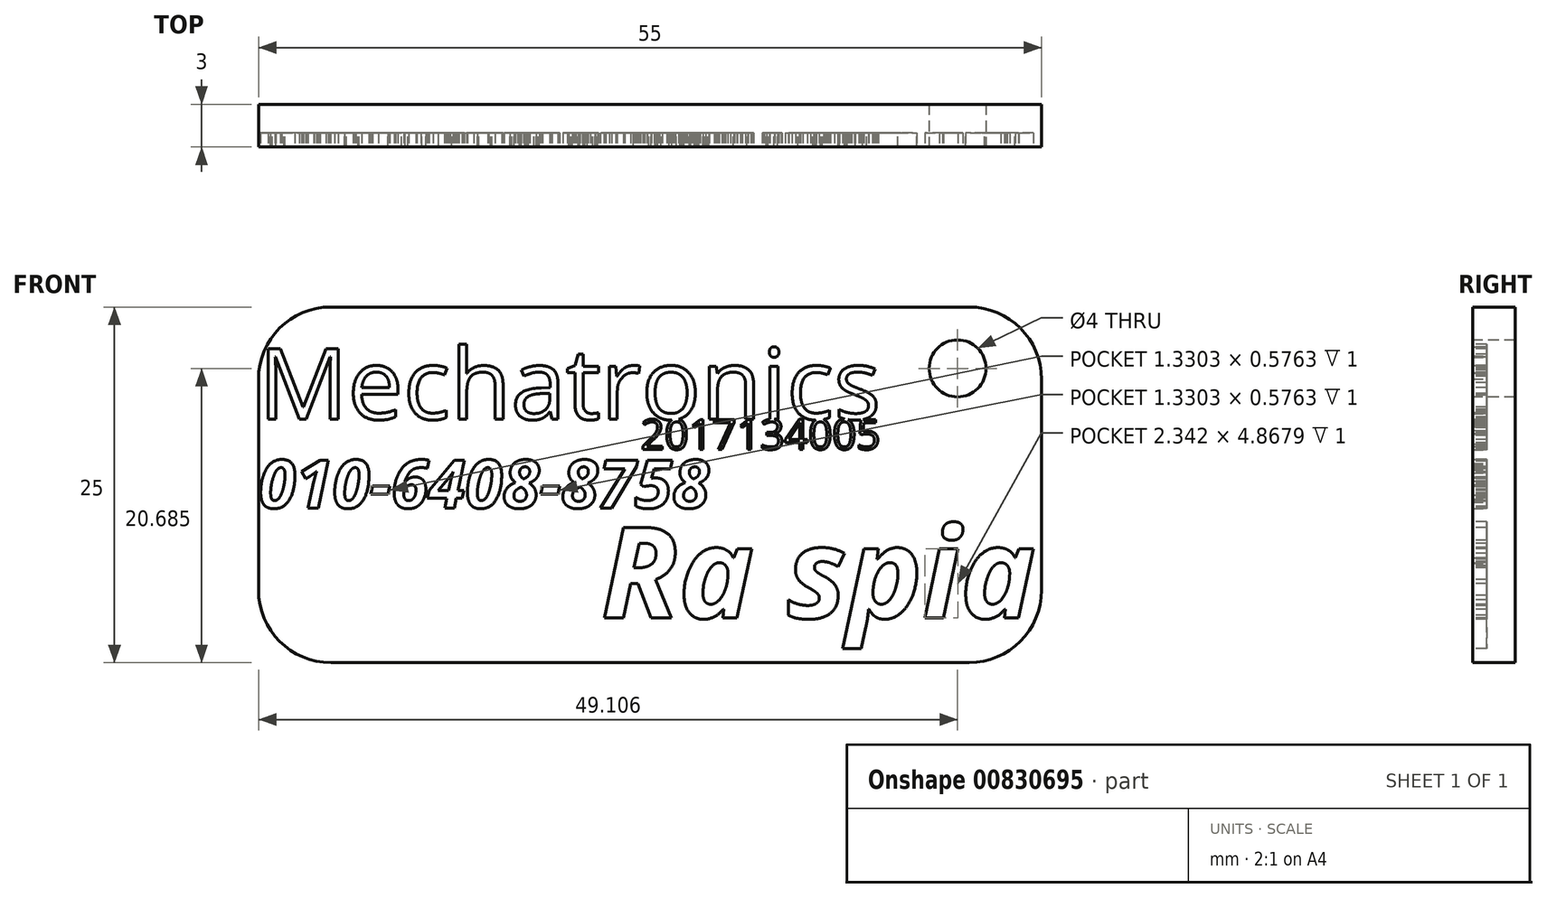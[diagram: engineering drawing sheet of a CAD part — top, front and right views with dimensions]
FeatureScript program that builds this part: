
annotation { "Feature Type Name" : "Feature", "Feature Type Description" : "" }
export const myFeature = defineFeature(function(context is Context, id is Id, definition is map)
    precondition{}
    {
        {
            var Q0;
            Q0=qCreatedBy(makeId("Front.planeOp"),FACE);
            var sketch = newSketch(context, id + "F0", { "sketchPlane" : qUnion([Q0])});
            skLineSegment(sketch, "E0.bottom", {"start": v(-24.07, 9.74) * mm, "end": v(30.93, 9.74) * mm});
            skLineSegment(sketch, "E0.top", {"start": v(-24.07, -15.26) * mm, "end": v(30.93, -15.26) * mm});
            skLineSegment(sketch, "E0.left", {"start": v(-24.07, 9.74) * mm, "end": v(-24.07, -15.26) * mm});
            skLineSegment(sketch, "E0.right", {"start": v(30.93, 9.74) * mm, "end": v(30.93, -15.26) * mm});
            skSolve(sketch);
        }
        {
            var Q0;
            Q0=makeQuery(id+"F0.imprint","IMPRINT",FACE,{"disambiguationData":[TD([[makeQuery(id+"F0.imprint","IMPRINT",EDGE,{"derivedFrom":sQuery(id+"F0.wireOp",EDGE,"E0.bottom")}),-1.0]])]});
            extrude(context, id + "F1", {"entities" : qUnion([Q0]), "depth" : 3 * mm, "offsetDistance" : 25.4 * mm});
        }
        {
            var Q0;
            Q0=makeQuery(id+"F1.opExtrude","CAP_FACE",FACE,{"disambiguationData":[OSD([sQuery(id+"F0.wireOp",EDGE,"E0.bottom"),sQuery(id+"F0.wireOp",EDGE,"E0.top"),sQuery(id+"F0.wireOp",EDGE,"E0.left"),sQuery(id+"F0.wireOp",EDGE,"E0.right")])],"isStart":false});
            var sketch = newSketch(context, id + "F2", { "sketchPlane" : qUnion([Q0])});
            skText(sketch, "E1", { "text": "010-6408-8758", "fontName": "OpenSans-BoldItalic.ttf"});
            skText(sketch, "E2", { "text": "Ra spia", "fontName": "OpenSans-BoldItalic.ttf"});
            skText(sketch, "E3", { "text": "Mechatronics", "fontName": "OpenSans-Regular.ttf"});
            skText(sketch, "E4", { "text": "2017134005", "fontName": "OpenSans-Regular.ttf"});
            const initialGuessF2  = {"E1": [-0.02407, -0.0044, 1, 0, 0.0034], "E2": [0, -0.01213, 1, 0, 0.00642], "E3": [-0.02407, 0.00185, 1, 0, 0.005], "E4": [0.00277, -0.00027, 1, 0, 0.00212]};
            skSetInitialGuess(sketch, initialGuessF2);
            skSolve(sketch);
        }
        {
            var Q0;
            Q0 = qSketchRegion(id + "F2", true);
            extrude(context, id + "F3", {"entities" : qUnion([Q0]), "operationType" : NewBodyOperationType.REMOVE, "oppositeDirection" : true, "depth" : 1 * mm, "offsetDistance" : 25.4 * mm});
        }
        {
            var Q0;
            Q0=makeQuery(id+"F1.opExtrude","SWEPT_EDGE",EDGE,{"disambiguationData":[OSD([sQuery(id+"F0.wireOp",EDGE,"E0.bottom"),sQuery(id+"F0.wireOp",EDGE,"E0.right")])]});
            fillet(context, id + "F4", {"entities" : qUnion([Q0]), "radius" : 5.08 * mm, "tangentPropagation" : true, "allowEdgeOverflow" : false});
        }
        {
            var Q0;
            Q0=makeQuery(id+"F1.opExtrude","SWEPT_EDGE",EDGE,{"disambiguationData":[OSD([sQuery(id+"F0.wireOp",EDGE,"E0.top"),sQuery(id+"F0.wireOp",EDGE,"E0.left")])]});
            fillet(context, id + "F5", {"entities" : qUnion([Q0]), "radius" : 5.08 * mm, "tangentPropagation" : true, "allowEdgeOverflow" : false});
        }
        {
            var Q0;
            Q0=makeQuery(id+"F1.opExtrude","SWEPT_EDGE",EDGE,{"disambiguationData":[OSD([sQuery(id+"F0.wireOp",EDGE,"E0.bottom"),sQuery(id+"F0.wireOp",EDGE,"E0.left")])]});
            fillet(context, id + "F6", {"entities" : qUnion([Q0]), "radius" : 5.08 * mm, "tangentPropagation" : true, "allowEdgeOverflow" : false});
        }
        {
            var Q0;
            Q0=makeQuery(id+"F1.opExtrude","SWEPT_EDGE",EDGE,{"disambiguationData":[OSD([sQuery(id+"F0.wireOp",EDGE,"E0.top"),sQuery(id+"F0.wireOp",EDGE,"E0.right")])]});
            fillet(context, id + "F7", {"entities" : qUnion([Q0]), "radius" : 5.08 * mm, "tangentPropagation" : true, "allowEdgeOverflow" : false});
        }
        {
            var Q0;
            {var subQ0=sQuery(id+"F0.wireOp",EDGE,"E0.left");var subQ1=sQuery(id+"F0.wireOp",EDGE,"E0.top");var subQ7=sQuery(id+"F0.wireOp",EDGE,"E0.bottom");var subQ11=sQuery(id+"F0.wireOp",EDGE,"E0.right");Q0=makeQuery(id+"F3.boolean.opBoolean","SPLIT",FACE,{"disambiguationData":[TD([makeQuery(id+"F1.opExtrude","SWEPT_FACE",FACE,{"disambiguationData":[OSD([subQ7])]})])],"derivedFrom":makeQuery(id+"F1.opExtrude","CAP_FACE",FACE,{"disambiguationData":[OSD([subQ7,subQ1,subQ0,subQ11])],"isStart":false})});}
            var sketch = newSketch(context, id + "F8", { "sketchPlane" : qUnion([Q0])});
            skCircle(sketch, "E5", {"center": v(25.04, 5.43) * mm, "radius": 2 * mm});
            skSolve(sketch);
        }
        {
            var Q0;
            Q0 = qSketchRegion(id + "F8", true);
            extrude(context, id + "F9", {"entities" : qUnion([Q0]), "operationType" : NewBodyOperationType.REMOVE, "oppositeDirection" : true, "depth" : 3 * mm, "offsetDistance" : 25.4 * mm});
        }
    });
